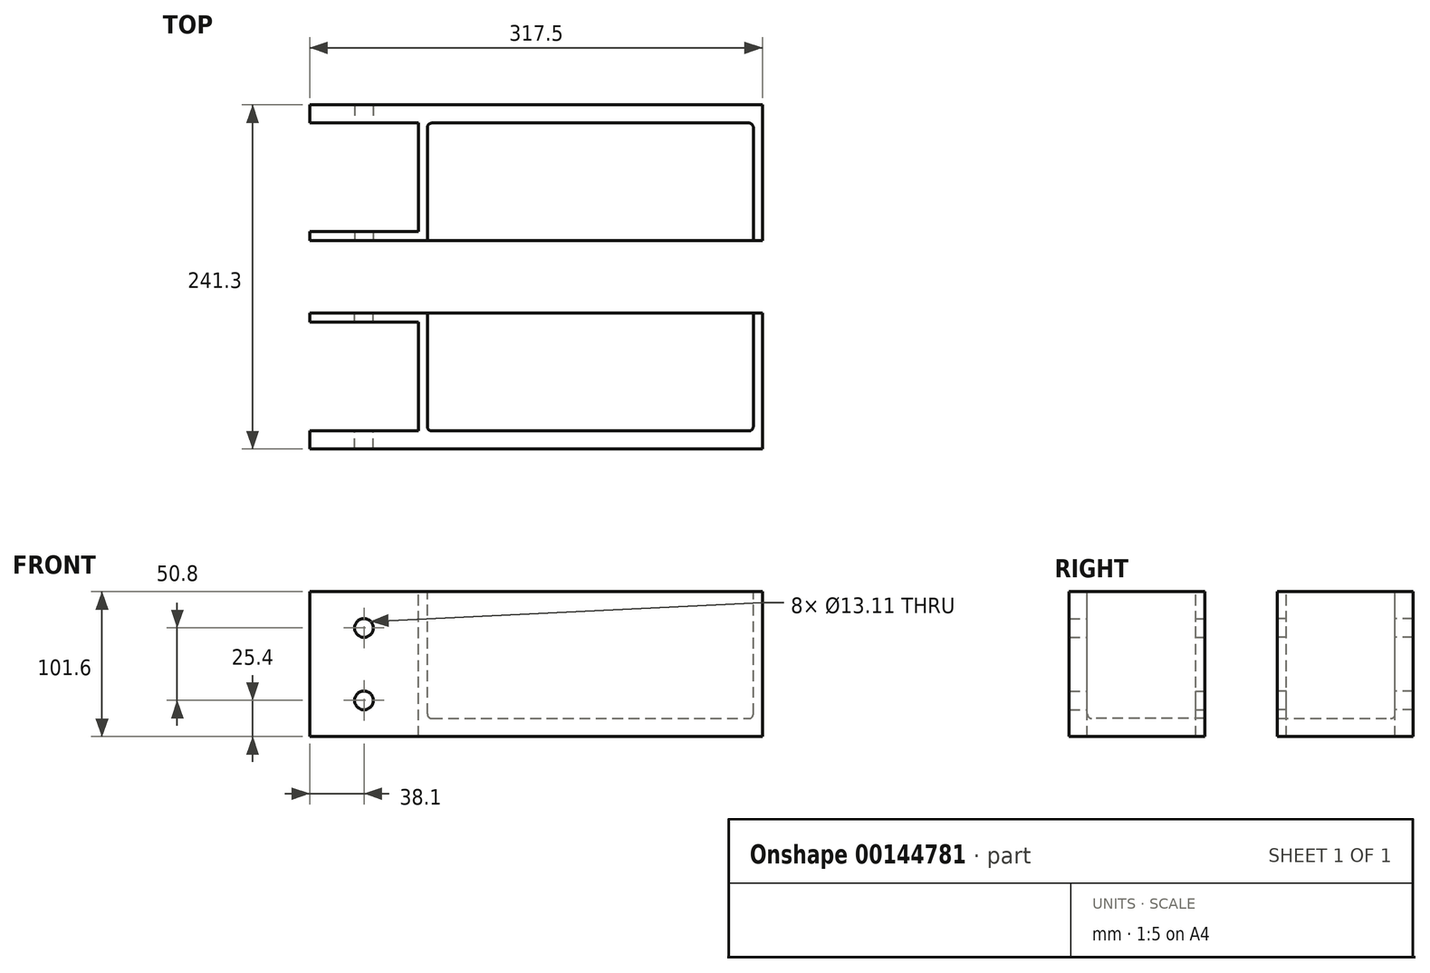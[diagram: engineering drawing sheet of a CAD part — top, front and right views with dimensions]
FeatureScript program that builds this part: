
annotation { "Feature Type Name" : "Feature", "Feature Type Description" : "" }
export const myFeature = defineFeature(function(context is Context, id is Id, definition is map)
    precondition{}
    {
        {
            var Q0;
            Q0=qCreatedBy(makeId("Front.planeOp"),FACE);
            var sketch = newSketch(context, id + "F0", { "sketchPlane" : qUnion([Q0])});
            skLineSegment(sketch, "E0.bottom", {"start": v(0, 0) * mm, "end": v(317.5, 0) * mm});
            skLineSegment(sketch, "E0.top", {"start": v(0, 101.6) * mm, "end": v(317.5, 101.6) * mm});
            skLineSegment(sketch, "E0.left", {"start": v(0, 0) * mm, "end": v(0, 101.6) * mm});
            skLineSegment(sketch, "E0.right", {"start": v(317.5, 0) * mm, "end": v(317.5, 101.6) * mm});
            skSolve(sketch);
        }
        {
            var Q0;
            Q0=qSketchRegion(id+"F0",true);
            extrude(context, id + "F1", {"entities" : qUnion([Q0]), "depth" : 95.25 * mm});
        }
        {
            var Q0;
            Q0=makeQuery(id+"F1.opExtrude","SWEPT_FACE",FACE,{"disambiguationData":[OSD([sQuery(id+"F0.wireOp",EDGE,"E0.top")])]});
            var sketch = newSketch(context, id + "F2", { "sketchPlane" : qUnion([Q0])});
            skLineSegment(sketch, "E1.bottom", {"start": v(0, -12.7) * mm, "end": v(76.2, -12.7) * mm});
            skLineSegment(sketch, "E1.top", {"start": v(0, -88.9) * mm, "end": v(76.2, -88.9) * mm});
            skLineSegment(sketch, "E1.left", {"start": v(0, -12.7) * mm, "end": v(0, -88.9) * mm});
            skLineSegment(sketch, "E1.right", {"start": v(76.2, -12.7) * mm, "end": v(76.2, -88.9) * mm});
            skSolve(sketch);
        }
        {
            var Q0;
            Q0=qSketchRegion(id+"F2",true);
            extrude(context, id + "F3", {"entities" : qUnion([Q0]), "operationType" : NewBodyOperationType.REMOVE, "endBound" : BoundingType.THROUGH_ALL, "oppositeDirection" : true, "depth" : 25.4 * mm});
        }
        {
            var Q0;
            Q0=makeQuery(id+"F1.opExtrude","SWEPT_FACE",FACE,{"disambiguationData":[OSD([sQuery(id+"F0.wireOp",EDGE,"E0.top")])]});
            var sketch = newSketch(context, id + "F4", { "sketchPlane" : qUnion([Q0])});
            skLineSegment(sketch, "E2.bottom", {"start": v(82.55, -95.25) * mm, "end": v(311.15, -95.25) * mm});
            skLineSegment(sketch, "E2.top", {"start": v(82.55, -12.7) * mm, "end": v(311.15, -12.7) * mm});
            skLineSegment(sketch, "E2.left", {"start": v(82.55, -95.25) * mm, "end": v(82.55, -12.7) * mm});
            skLineSegment(sketch, "E2.right", {"start": v(311.15, -95.25) * mm, "end": v(311.15, -12.7) * mm});
            skSolve(sketch);
        }
        {
            var Q0;
            Q0=qSketchRegion(id+"F4",true);
            extrude(context, id + "F5", {"entities" : qUnion([Q0]), "operationType" : NewBodyOperationType.REMOVE, "oppositeDirection" : true, "depth" : 88.9 * mm});
        }
        {
            var Q0;
            Q0=makeQuery(id+"F5.boolean.opBoolean","COPY",EDGE,{"derivedFrom":makeQuery(id+"F5.opExtrude","CAP_EDGE",EDGE,{"disambiguationData":[OSD([sQuery(id+"F4.wireOp",EDGE,"E2.left")])],"isStart":false})});
            var Q1;
            Q1=makeQuery(id+"F5.boolean.opBoolean","COPY",EDGE,{"derivedFrom":makeQuery(id+"F5.opExtrude","CAP_EDGE",EDGE,{"disambiguationData":[OSD([sQuery(id+"F4.wireOp",EDGE,"E2.top")])],"isStart":false})});
            var Q2;
            Q2=makeQuery(id+"F5.boolean.opBoolean","COPY",EDGE,{"derivedFrom":makeQuery(id+"F5.opExtrude","CAP_EDGE",EDGE,{"disambiguationData":[OSD([sQuery(id+"F4.wireOp",EDGE,"E2.right")])],"isStart":false})});
            var Q3;
            Q3=makeQuery(id+"F5.boolean.opBoolean","COPY",EDGE,{"derivedFrom":makeQuery(id+"F5.opExtrude","SWEPT_EDGE",EDGE,{"disambiguationData":[OSD([sQuery(id+"F4.wireOp",EDGE,"E2.top"),sQuery(id+"F4.wireOp",EDGE,"E2.right")])]})});
            var Q4;
            Q4=makeQuery(id+"F5.boolean.opBoolean","COPY",EDGE,{"derivedFrom":makeQuery(id+"F5.opExtrude","SWEPT_EDGE",EDGE,{"disambiguationData":[OSD([sQuery(id+"F4.wireOp",EDGE,"E2.top"),sQuery(id+"F4.wireOp",EDGE,"E2.left")])]})});
            fillet(context, id + "F6", {"entities" : qUnion([Q0, Q1, Q2, Q3, Q4]), "radius" : 3.17 * mm, "tangentPropagation" : true, "allowEdgeOverflow" : false});
        }
        {
            var Q0;
            Q0=makeQuery(id+"F1.opExtrude","CAP_FACE",FACE,{"disambiguationData":[OSD([sQuery(id+"F0.wireOp",EDGE,"E0.bottom"),sQuery(id+"F0.wireOp",EDGE,"E0.top"),sQuery(id+"F0.wireOp",EDGE,"E0.left"),sQuery(id+"F0.wireOp",EDGE,"E0.right")])],"isStart":false});
            var sketch = newSketch(context, id + "F7", { "sketchPlane" : qUnion([Q0])});
            skLineSegment(sketch, "E3", {"start": v(38.1, 101.6) * mm, "end": v(38.1, 0) * mm, "construction": true});
            skPoint(sketch, "E4", {"position": v(38.1, 76.2) * mm});
            skPoint(sketch, "E5", {"position": v(38.1, 25.4) * mm});
            skSolve(sketch);
        }
        {
            var Q0;
            Q0=sQuery(id+"F7.wireOp",VERTEX,"E4");
            var Q1;
            Q1=sQuery(id+"F7.wireOp",VERTEX,"E5");
            var Q2;
            Q2=makeQuery(id+"F1.opExtrude","SWEPT_BODY",BODY,{"disambiguationData":[OSD([sQuery(id+"F0.wireOp",EDGE,"E0.bottom"),sQuery(id+"F0.wireOp",EDGE,"E0.top"),sQuery(id+"F0.wireOp",EDGE,"E0.left"),sQuery(id+"F0.wireOp",EDGE,"E0.right")])]});
            hole(context, id + "F8", {"style" : HoleStyle.SIMPLE, "endStyle" : HoleEndStyle.THROUGH, "standardTappedOrClearance" : lookupTablePath({ "standard" : "ANSI", "fit" : "Close", "size" : "1/2", "type" : "Clearance" }), "standardBlindInLast" : lookupTablePath({ "fit" : "Close", "standard" : "ANSI", "size" : "1/2", "type" : "Clearance" }), "holeDiameter" : 13.1 * mm, "locations" : qUnion([Q0, Q1]), "scope" : qUnion([Q2]), "isTappedThrough" : true});
        }
        {
            var Q0;
            Q0=makeQuery(id+"F1.opExtrude","CAP_FACE",FACE,{"disambiguationData":[OSD([sQuery(id+"F0.wireOp",EDGE,"E0.bottom"),sQuery(id+"F0.wireOp",EDGE,"E0.top"),sQuery(id+"F0.wireOp",EDGE,"E0.left"),sQuery(id+"F0.wireOp",EDGE,"E0.right")])],"isStart":false});
            cPlane(context, id + "F9", {"entities" : qUnion([Q0]), "cplaneType" : CPlaneType.OFFSET, "offset" : 25.4 * mm, "width" : 152.4 * mm, "height" : 152.4 * mm});
        }
        {
            var Q0;
            Q0=makeQuery(id+"F1.opExtrude","SWEPT_BODY",BODY,{"disambiguationData":[OSD([sQuery(id+"F0.wireOp",EDGE,"E0.bottom"),sQuery(id+"F0.wireOp",EDGE,"E0.top"),sQuery(id+"F0.wireOp",EDGE,"E0.left"),sQuery(id+"F0.wireOp",EDGE,"E0.right")])]});
            var Q1;
            Q1=qCreatedBy(id+"F9.planeOp",FACE);
            mirror(context, id + "F10", {"entities" : qUnion([Q0]), "mirrorPlane" : qUnion([Q1])});
        }
    });
